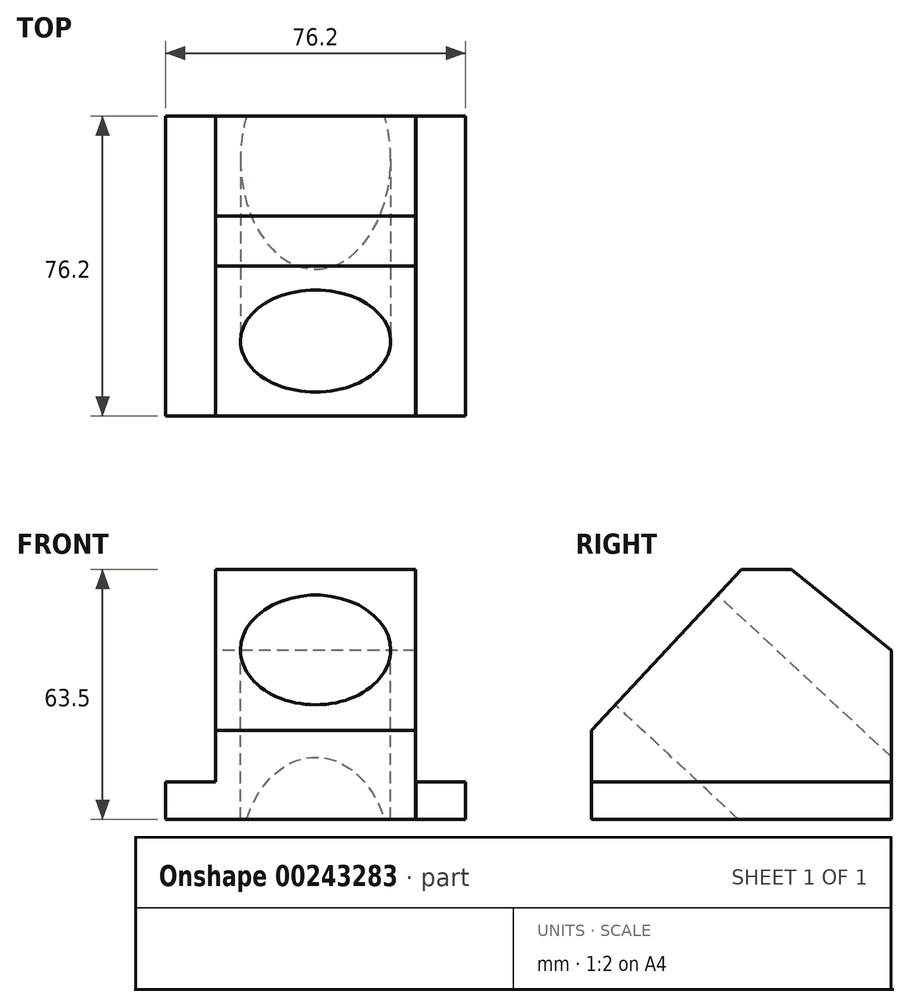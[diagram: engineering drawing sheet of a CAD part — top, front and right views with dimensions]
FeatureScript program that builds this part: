
annotation { "Feature Type Name" : "Feature", "Feature Type Description" : "" }
export const myFeature = defineFeature(function(context is Context, id is Id, definition is map)
    precondition{}
    {
        {
            var Q0;
            Q0=qCreatedBy(makeId("Top.planeOp"),FACE);
            var sketch = newSketch(context, id + "F0", { "sketchPlane" : qUnion([Q0])});
            skLineSegment(sketch, "E0.bottom", {"start": v(-37.68, 34.51) * mm, "end": v(38.52, 34.51) * mm});
            skLineSegment(sketch, "E0.top", {"start": v(-37.68, -41.69) * mm, "end": v(38.52, -41.69) * mm});
            skLineSegment(sketch, "E0.left", {"start": v(-37.68, 34.51) * mm, "end": v(-37.68, -41.69) * mm});
            skLineSegment(sketch, "E0.right", {"start": v(38.52, 34.51) * mm, "end": v(38.52, -41.69) * mm});
            skLineSegment(sketch, "E1.bottom", {"start": v(-24.9, 34.51) * mm, "end": v(25.9, 34.51) * mm});
            skLineSegment(sketch, "E1.top", {"start": v(-24.9, -41.69) * mm, "end": v(25.9, -41.69) * mm});
            skLineSegment(sketch, "E1.left", {"start": v(-24.9, 34.51) * mm, "end": v(-24.9, -41.69) * mm});
            skLineSegment(sketch, "E1.right", {"start": v(25.9, 34.51) * mm, "end": v(25.9, -41.69) * mm});
            skSolve(sketch);
        }
        {
            var Q0;
            {var subQ0=sQuery(id+"F0.wireOp",EDGE,"E0.left");Q0=makeQuery(id+"F0.imprint","IMPRINT",FACE,{"disambiguationData":[TD([[makeQuery(id+"F0.imprint","IMPRINT",EDGE,{"derivedFrom":subQ0}),1.0]])]});}
            var Q1;
            {var subQ0=sQuery(id+"F0.wireOp",EDGE,"E0.right");Q1=makeQuery(id+"F0.imprint","IMPRINT",FACE,{"disambiguationData":[TD([[makeQuery(id+"F0.imprint","IMPRINT",EDGE,{"derivedFrom":subQ0}),-1.0]])]});}
            var Q2;
            Q2=makeQuery(id+"F0.imprint","IMPRINT",FACE,{"disambiguationData":[TD([[makeQuery(id+"F0.imprint","IMPRINT",EDGE,{"derivedFrom":sQuery(id+"F0.wireOp",EDGE,"E1.bottom")}),-1.0]])]});
            extrude(context, id + "F1", {"entities" : qUnion([Q0, Q1, Q2]), "depth" : 9.52 * mm});
        }
        {
            var Q0;
            Q0=makeQuery(id+"F1.opExtrude","CAP_FACE",FACE,{"disambiguationData":[OSD([sQuery(id+"F0.wireOp",EDGE,"E0.bottom"),sQuery(id+"F0.wireOp",EDGE,"E0.top"),sQuery(id+"F0.wireOp",EDGE,"E0.left"),sQuery(id+"F0.wireOp",EDGE,"E0.right"),sQuery(id+"F0.wireOp",EDGE,"E1.bottom"),sQuery(id+"F0.wireOp",EDGE,"E1.top")])],"isStart":true});
            var sketch = newSketch(context, id + "F2", { "sketchPlane" : qUnion([Q0])});
            skLineSegment(sketch, "E2.bottom", {"start": v(-24.98, 41.69) * mm, "end": v(25.82, 41.69) * mm});
            skLineSegment(sketch, "E2.top", {"start": v(-24.98, -34.51) * mm, "end": v(25.82, -34.51) * mm});
            skLineSegment(sketch, "E2.left", {"start": v(-24.98, 41.69) * mm, "end": v(-24.98, -34.51) * mm});
            skLineSegment(sketch, "E2.right", {"start": v(25.82, 41.69) * mm, "end": v(25.82, -34.51) * mm});
            skSolve(sketch);
        }
        {
            var Q0;
            Q0 = qSketchRegion(id + "F2", true);
            extrude(context, id + "F3", {"entities" : qUnion([Q0]), "operationType" : NewBodyOperationType.ADD, "oppositeDirection" : true, "depth" : 63.5 * mm});
        }
        {
            var Q0;
            Q0=makeQuery(id+"F3.opExtrude","SWEPT_FACE",FACE,{"disambiguationData":[OSD([sQuery(id+"F2.wireOp",EDGE,"E2.left")])]});
            var sketch = newSketch(context, id + "F4", { "sketchPlane" : qUnion([Q0])});
            skLineSegment(sketch, "E3", {"start": v(-34.51, 42.88) * mm, "end": v(-9.11, 63.5) * mm});
            skLineSegment(sketch, "E4", {"start": v(-9.11, 63.5) * mm, "end": v(3.59, 63.5) * mm});
            skLineSegment(sketch, "E5", {"start": v(3.59, 63.5) * mm, "end": v(41.69, 22.64) * mm});
            skLineSegment(sketch, "E6", {"start": v(41.69, 22.64) * mm, "end": v(41.69, 63.5) * mm});
            skLineSegment(sketch, "E7", {"start": v(41.69, 63.5) * mm, "end": v(3.59, 63.5) * mm});
            skLineSegment(sketch, "E8", {"start": v(-9.11, 63.5) * mm, "end": v(-34.51, 63.5) * mm});
            skLineSegment(sketch, "E9", {"start": v(-34.51, 63.5) * mm, "end": v(-34.51, 42.88) * mm});
            skSolve(sketch);
        }
        {
            var Q0;
            Q0 = qSketchRegion(id + "F4", true);
            extrude(context, id + "F5", {"entities" : qUnion([Q0]), "operationType" : NewBodyOperationType.REMOVE, "oppositeDirection" : true, "depth" : 107.7 * mm});
        }
        {
            var Q0;
            Q0=makeQuery(id+"F5.boolean.opBoolean","COPY",FACE,{"derivedFrom":makeQuery(id+"F5.opExtrude","SWEPT_FACE",FACE,{"disambiguationData":[OSD([sQuery(id+"F4.wireOp",EDGE,"E5")])]})});
            var sketch = newSketch(context, id + "F6", { "sketchPlane" : qUnion([Q0])});
            skCircle(sketch, "E10", {"center": v(0.42, 16.06) * mm, "radius": 19.05 * mm});
            skPoint(sketch, "E11.orphan", {"position": v(0.42, 44) * mm});
            skPoint(sketch, "E12.end.orphan", {"position": v(0.42, -11.87) * mm});
            skPoint(sketch, "E13.orphan", {"position": v(-24.98, 16.06) * mm});
            skPoint(sketch, "E14.end.orphan", {"position": v(25.82, 16.06) * mm});
            skLineSegment(sketch, "E15", {"start": v(-24.98, 44) * mm, "end": v(25.82, 44) * mm});
            skLineSegment(sketch, "E16", {"start": v(25.82, 44) * mm, "end": v(25.82, -11.87) * mm});
            skLineSegment(sketch, "E17", {"start": v(25.82, -11.87) * mm, "end": v(-24.98, -11.87) * mm});
            skLineSegment(sketch, "E18", {"start": v(-24.98, -11.87) * mm, "end": v(-24.98, 44) * mm});
            skSolve(sketch);
        }
        {
            var Q0;
            Q0=makeQuery(id+"F6.imprint","IMPRINT",FACE,{"disambiguationData":[TD([[makeQuery(id+"F6.imprint","IMPRINT",EDGE,{"derivedFrom":sQuery(id+"F6.wireOp",EDGE,"E10")}),1.0]])]});
            extrude(context, id + "F7", {"entities" : qUnion([Q0]), "operationType" : NewBodyOperationType.REMOVE, "oppositeDirection" : true, "depth" : 89.66 * mm});
        }
    });
